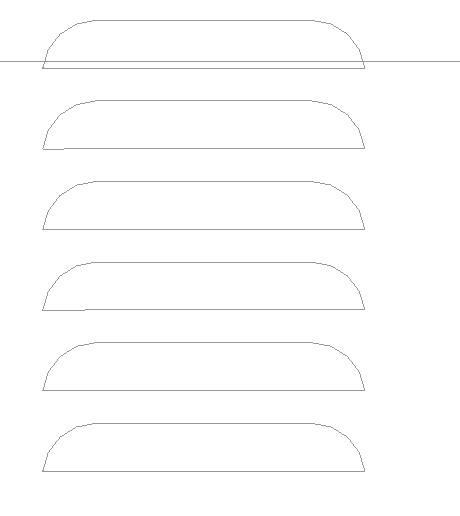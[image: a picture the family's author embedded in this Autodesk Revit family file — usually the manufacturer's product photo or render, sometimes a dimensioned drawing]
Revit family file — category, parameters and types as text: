
# Revit family: AquaMaster-Inverter_ENG-RFA-2022
name_source: partatom
category: Mechanické zařízení
units: mm (PartAtom-declared; Revit-internal decimal feet)

## family parameters
Bod výpočtu místnosti = Ne
Kóta kulaté spojky = Použít průměr
Nadpis OmniClass = Climate Control (HVAC)
Ořezat dutým tvarem při načtení = Ne
Sdílené = Ne
Typ dílu = Normální
Vždy vertikální = Ano
Zachovat orientaci poznámky = Ne
Založené na pracovní rovině = Ne
Číslo OmniClass = 23.75.00.00

## types (8) — shared parameters
MT_active power = 0 W
MT_angle offset = 60 mm  [stored 0.19685 ft]
MT_apparent power = 0 VA
MT_case mat = MT_RAL9006
MT_clearance back = 200 mm  [stored 0.656168 ft]
MT_clearance front = 600 mm
MT_frequency (Hz) = 50 Hz
MT_pipe connector mat = MT_RGB-130-130-130
MT_pipe mat = MT_angle-corner
Popis = Ground-to-water heat pump
Výrobce = Master Therm
zero-valued in all types: Cena, MT_CosPhi, Výchozí výška

## per-type parameters (varying)
- AQ45I: CI_hot water – inlet=1'' (OD); CO_hot water – outlet=1'' (OD); Desuperheater – inlet/outlet=not available; EI_brine – inlet=5/4'' (OD); EO_brine – outlet=5/4'' (OD); El. connection=2xPG16; 4xPG13.5; Komentáře k typům=COMPRESSOR: BLDC Inverter; 30 – 90 rps; charge of POE oil – 1.3 l; max. op. current – 15 A; EVAPORATOR: PHE; AISI316; water flow (W/W) – 1.62 kg/s; min. flow – 1.48 kg/s; brine flow (B/W) – 0.89 kg/s; min. flow – 0.54 kg/s; temp. difference – 3 K; int. volume – 5.1 l; pump ext. head – 3.5 m; pump motor – 250 W; CONDENSER: PHE; AISI316; water flow – 0.62 kg/s; min. flow – 0.46 kg/s; temp. difference – 5 K; int. volume – 4.1 l; pump ext. head – 3.0 m; pump motor – 100 W; REFRIGERANT CIRCUIT: R410a (2.4 kg); AUX. HEATER (optional): 7.5 kW; CONTROLS: controller – pCO5; EEV – yes; water probe – yes; SHW probe/output – yes (2x); mixing probe/output – yes; outdoor probe – yes; dynamic set point – yes; refrigerant probe – 2xPT; POWER SUPPLY: 3x400 V; 50 Hz; max. current – 20 A; max. current, incl. aux. heater – 28 A; DIMENSIONS: hot water, brine – 1", 5/4" (OD); 120x56x72 cm; 170 kg; LIMITS: max. water overpress. – 0.25 MPa; max. refr. overpress. – 4.2 MPa; brine min./max.: -5/+20 °C; water min./max.: 20/60 °C; MT_CI diameter=28 mm  [stored 0.0918635 ft]; MT_CI offset_X=73 mm  [stored 0.239501 ft]; MT_CO diameter=28 mm  [stored 0.0918635 ft]; MT_CO offset_X=173 mm  [stored 0.567585 ft]; MT_EC AQ17I_YES=Ne; MT_EC-AQ90I_YES=Ne; MT_EC1 offset_X=25 mm  [stored 0.082021 ft]; MT_EC1 offset_Y=90 mm  [stored 0.295276 ft]; MT_EC2 offset_X=25 mm  [stored 0.082021 ft]; MT_EC2 offset_Y=60 mm  [stored 0.19685 ft]; MT_EC3 offset_X=25 mm  [stored 0.082021 ft]; MT_EC3 offset_Y=30 mm  [stored 0.0984252 ft]; MT_EC4 offset_X=421 mm  [stored 1.38123 ft]; MT_EC4 offset_Y=90 mm  [stored 0.295276 ft]; MT_EC5 offset_X=421 mm  [stored 1.38123 ft]; MT_EC5 offset_Y=60 mm  [stored 0.19685 ft]; MT_EC6 offset_X=421 mm  [stored 1.38123 ft]; MT_EC6 offset_Y=30 mm  [stored 0.0984252 ft]; MT_EC6_YES=Ano; MT_EI diameter=35 mm  [stored 0.114829 ft]; MT_EI offset_X=373 mm  [stored 1.22375 ft]; MT_EO diameter=35 mm  [stored 0.114829 ft]; MT_EO offset_X=273 mm  [stored 0.895669 ft]; MT_TYPE=45; MT_angle length_X=406 mm  [stored 1.33202 ft]; MT_angle length_Y=596 mm; MT_angle length_Z=1080 mm; MT_case depth=716 mm; MT_case height=1200 mm; MT_case width=526 mm  [stored 1.72572 ft]; MT_clearance left=400 mm  [stored 1.31234 ft]; MT_clearance right=400 mm  [stored 1.31234 ft]; MT_clearance top=1800 mm; MT_cover front_X=446 mm  [stored 1.46325 ft]; MT_cover front_Y=1120 mm; MT_cover side_X=636 mm; MT_cover side_Y=1120 mm; MT_cover top_X=446 mm  [stored 1.46325 ft]; MT_cover top_Y=636 mm; MT_desuperheater diameter=0 mm  [stored 0 ft]; MT_desuperheater offset_X=223 mm  [stored 0.731627 ft]; MT_desuperheater_YES=Ne; MT_lock offset_V=300 mm; MT_lower vent grille_YES=Ne; MT_max. current, incl. aux. heater (A)=28 A; MT_pipe connector angle=0.00°; MT_pipe connector offset=486 mm; MT_pipe connector_X=446 mm  [stored 1.46325 ft]; MT_pipe connector_Y=120 mm  [stored 0.393701 ft]; MT_pivot offset=0 mm  [stored 0 ft]; MT_power switch_YES=Ano; MT_upper center lock_YES=Ano; MT_upper vent grille offset_H=175 mm  [stored 0.574147 ft]; MT_upper vent grille offset_V=200 mm  [stored 0.656168 ft]; MT_vent grille_YES=Ano; MT_voltage (V)=400 V; MT_weight (kg)=170; Model=AquaMaster Inverter 45I; URL=https://mastertherm.cz
- AQ60I: CI_hot water – inlet=1'' (OD); CO_hot water – outlet=1'' (OD); Desuperheater – inlet/outlet=not available; EI_brine – inlet=5/4'' (OD); EO_brine – outlet=5/4'' (OD); El. connection=2xPG16; 4xPG13.5; Komentáře k typům=COMPRESSOR: BLDC Inverter Scroll; 30 – 100 rps; charge of POE oil – 1.4 l; max. op. current – 35 A; EVAPORATOR: PHE; AISI316; water flow (W/W) – 2.37 kg/s; min. flow – 2.09 kg/s; brine flow (B/W) – 1.31 kg/s; min. flow – 0.79 kg/s; temp. difference – 3 K; int. volume – 5.1 l; pump ext. head – 5.0 m; pump motor – 450 W; CONDENSER: PHE; AISI316; water flow – 0.92 kg/s; min. flow – 0.69 kg/s; temp. difference – 5 K; int. volume – 4.1 l; pump ext. head – 3.0 m; pump motor – 130 W; REFRIGERANT CIRCUIT: R410a (2.5 kg); AUX. HEATER (optional): 7.5 kW; CONTROLS: controller – pCO5; EEV – 1+1 (EVI); water probe – yes; SHW probe/output – yes (2x); mixing probe/output – yes; outdoor probe – yes; dynamic set point – yes; refrigerant probe – 2xPT; POWER SUPPLY: 3x400 V; 50 Hz; max. current – 25 A; max. current, incl. aux. heater – 35 A; DIMENSIONS: hot water, brine – 1", 5/4" (OD); 120x56x72 cm; 190 kg; LIMITS: max. water overpress. – 0.25 MPa; max. refr. overpress. – 4.2 MPa; brine min./max.: -5/+20 °C; water min./max.: 20/60 °C; MT_CI diameter=28 mm  [stored 0.0918635 ft]; MT_CI offset_X=73 mm  [stored 0.239501 ft]; MT_CO diameter=28 mm  [stored 0.0918635 ft]; MT_CO offset_X=173 mm  [stored 0.567585 ft]; MT_EC AQ17I_YES=Ne; MT_EC-AQ90I_YES=Ne; MT_EC1 offset_X=25 mm  [stored 0.082021 ft]; MT_EC1 offset_Y=90 mm  [stored 0.295276 ft]; MT_EC2 offset_X=25 mm  [stored 0.082021 ft]; MT_EC2 offset_Y=60 mm  [stored 0.19685 ft]; MT_EC3 offset_X=25 mm  [stored 0.082021 ft]; MT_EC3 offset_Y=30 mm  [stored 0.0984252 ft]; MT_EC4 offset_X=421 mm  [stored 1.38123 ft]; MT_EC4 offset_Y=90 mm  [stored 0.295276 ft]; MT_EC5 offset_X=421 mm  [stored 1.38123 ft]; MT_EC5 offset_Y=60 mm  [stored 0.19685 ft]; MT_EC6 offset_X=421 mm  [stored 1.38123 ft]; MT_EC6 offset_Y=30 mm  [stored 0.0984252 ft]; MT_EC6_YES=Ano; MT_EI diameter=35 mm  [stored 0.114829 ft]; MT_EI offset_X=373 mm  [stored 1.22375 ft]; MT_EO diameter=35 mm  [stored 0.114829 ft]; MT_EO offset_X=273 mm  [stored 0.895669 ft]; MT_TYPE=60; MT_angle length_X=406 mm  [stored 1.33202 ft]; MT_angle length_Y=596 mm; MT_angle length_Z=1080 mm; MT_case depth=716 mm; MT_case height=1200 mm; MT_case width=526 mm  [stored 1.72572 ft]; MT_clearance left=400 mm  [stored 1.31234 ft]; MT_clearance right=400 mm  [stored 1.31234 ft]; MT_clearance top=1800 mm; MT_cover front_X=446 mm  [stored 1.46325 ft]; MT_cover front_Y=1120 mm; MT_cover side_X=636 mm; MT_cover side_Y=1120 mm; MT_cover top_X=446 mm  [stored 1.46325 ft]; MT_cover top_Y=636 mm; MT_desuperheater diameter=0 mm  [stored 0 ft]; MT_desuperheater offset_X=223 mm  [stored 0.731627 ft]; MT_desuperheater_YES=Ne; MT_lock offset_V=300 mm; MT_lower vent grille_YES=Ne; MT_max. current, incl. aux. heater (A)=35 A; MT_pipe connector angle=0.00°; MT_pipe connector offset=486 mm; MT_pipe connector_X=446 mm  [stored 1.46325 ft]; MT_pipe connector_Y=120 mm  [stored 0.393701 ft]; MT_pivot offset=0 mm  [stored 0 ft]; MT_power switch_YES=Ano; MT_upper center lock_YES=Ano; MT_upper vent grille offset_H=175 mm  [stored 0.574147 ft]; MT_upper vent grille offset_V=200 mm  [stored 0.656168 ft]; MT_vent grille_YES=Ano; MT_voltage (V)=400 V; MT_weight (kg)=190; Model=AquaMaster Inverter 60I; URL=https://mastertherm.cz
- AQ90I: CI_hot water – inlet=5/4'' (OD); CO_hot water – outlet=5/4'' (OD); Desuperheater – inlet/outlet=2xCu Ø15 mm (ID); EI_brine – inlet=5/4'' (OD); EO_brine – outlet=5/4'' (OD); El. connection=2xPG21; 2xPG16; 4xPG13.5; Komentáře k typům=COMPRESSOR: BLDC Inverter Scroll; 30 – 150 rps; charge of POE oil – 1.4 l; max. op. current – 35 A; EVAPORATOR: PHE; AISI316; water flow (W/W) – 3.64 kg/s; min. flow – 3.15 kg/s; brine flow (B/W) – 2.09 kg/s; min. flow – 1.26 kg/s; temp. difference – 3 K; int. volume – 5.1 l; pump ext. head – 5.0 m; pump motor – 310 W; CONDENSER: PHE; AISI316; water flow – 1.50 kg/s; min. flow – 1.12 kg/s; temp. difference – 5 K; int. volume – 4.1 l; pump ext. head – 8.0 m; pump motor – 310 W; REFRIGERANT CIRCUIT: R410a (4.0 kg); AUX. HEATER (optional): 7.5 kW; CONTROLS: controller – pCO5; EEV – 1+1 (EVI); water probe – yes; SHW probe/output – yes (2x); mixing probe/output – yes; outdoor probe – yes; dynamic set point – yes; refrigerant probe – 2xPT; POWER SUPPLY: 3x400 V; 50 Hz; max. current – 40 A; max. current, incl. aux. heater – 50 A; DIMENSIONS: hot water, brine – 5/4", 5/4" (OD); 120x72x72 cm; 210 kg; LIMITS: max. water overpress. – 0.25 MPa; max. refr. overpress. – 4.2 MPa; brine min./max.: -5/+20 °C; water min./max.: 20/60 °C; MT_CI diameter=35 mm  [stored 0.114829 ft]; MT_CI offset_X=93 mm  [stored 0.305118 ft]; MT_CO diameter=35 mm  [stored 0.114829 ft]; MT_CO offset_X=243 mm  [stored 0.797244 ft]; MT_EC AQ17I_YES=Ne; MT_EC-AQ90I_YES=Ano; MT_EC1 offset_X=25 mm  [stored 0.082021 ft]; MT_EC1 offset_Y=90 mm  [stored 0.295276 ft]; MT_EC2 offset_X=25 mm  [stored 0.082021 ft]; MT_EC2 offset_Y=60 mm  [stored 0.19685 ft]; MT_EC3 offset_X=25 mm  [stored 0.082021 ft]; MT_EC3 offset_Y=30 mm  [stored 0.0984252 ft]; MT_EC4 offset_X=608 mm; MT_EC4 offset_Y=90 mm  [stored 0.295276 ft]; MT_EC5 offset_X=608 mm; MT_EC5 offset_Y=60 mm  [stored 0.19685 ft]; MT_EC6 offset_X=608 mm; MT_EC6 offset_Y=30 mm  [stored 0.0984252 ft]; MT_EC6_YES=Ano; MT_EI diameter=35 mm  [stored 0.114829 ft]; MT_EI offset_X=543 mm  [stored 1.7815 ft]; MT_EO diameter=35 mm  [stored 0.114829 ft]; MT_EO offset_X=393 mm  [stored 1.28937 ft]; MT_TYPE=90; MT_angle length_X=596 mm; MT_angle length_Y=596 mm; MT_angle length_Z=1080 mm; MT_case depth=716 mm; MT_case height=1200 mm; MT_case width=716 mm; MT_clearance left=400 mm  [stored 1.31234 ft]; MT_clearance right=400 mm  [stored 1.31234 ft]; MT_clearance top=1800 mm; MT_cover front_X=636 mm; MT_cover front_Y=1120 mm; MT_cover side_X=636 mm; MT_cover side_Y=1120 mm; MT_cover top_X=636 mm; MT_cover top_Y=636 mm; MT_desuperheater diameter=15 mm  [stored 0.0492126 ft]; MT_desuperheater offset_X=318 mm  [stored 1.04331 ft]; MT_desuperheater_YES=Ano; MT_lock offset_V=300 mm; MT_lower vent grille_YES=Ne; MT_max. current, incl. aux. heater (A)=50 A; MT_pipe connector angle=0.00°; MT_pipe connector offset=676 mm; MT_pipe connector_X=636 mm; MT_pipe connector_Y=120 mm  [stored 0.393701 ft]; MT_pivot offset=0 mm  [stored 0 ft]; MT_power switch_YES=Ano; MT_upper center lock_YES=Ano; MT_upper vent grille offset_H=175 mm  [stored 0.574147 ft]; MT_upper vent grille offset_V=200 mm  [stored 0.656168 ft]; MT_vent grille_YES=Ne; MT_voltage (V)=400 V; MT_weight (kg)=210; Model=AquaMaster Inverter 90I; URL=https://www.mastertherm.eu
- AQ17I: CI_hot water – inlet=1'' (OD); CO_hot water – outlet=1'' (OD); Desuperheater – inlet/outlet=not available; EI_brine – inlet=1'' (OD); EO_brine – outlet=1'' (OD); El. connection=2xPG16; 4xPG13.5; Komentáře k typům=COMPRESSOR: BLDC Inverter; 15 – 65 rps; charge of POE oil – 0.9 l; max. op. current – 16 A; EVAPORATOR: PHE; AISI316; water flow (W/W) – 0.38 kg/s; min. flow – 0.28 kg/s; brine flow (B/W) – 0.19 kg/s; min. flow – 0.11 kg/s; temp. difference – 3 K; int. volume – 2.0 l; pump ext. head – 7.0 m; pump motor – 70 W; CONDENSER: PHE; AISI316; water flow – 0.14 kg/s; min. flow – 0.09 kg/s; temp. difference – 5 K; int. volume – 4.1 l; pump ext. head – 7.0 m; pump motor – 70 W; REFRIGERANT CIRCUIT: R410a (0.75 kg); AUX. HEATER (optional): not available; CONTROLS: controller – uPC; EEV – yes; water probe – yes; SHW probe/output – no; mixing probe/output – yes; outdoor probe – yes; dynamic set point – yes; refrigerant probe – 2xPT; POWER SUPPLY: 1x230 V; 50 Hz; max. current – 16 A; DIMENSIONS: hot water, brine – 1", 1" (OD); 82x53x53 cm; 60 kg; LIMITS: max. water overpress. – 0.25 MPa; max. refr. overpress. – 4.2 MPa; brine min./max.: -5/+20 °C; water min./max.: 20/60 °C; MT_CI diameter=28 mm  [stored 0.0918635 ft]; MT_CI offset_X=440 mm  [stored 1.44357 ft]; MT_CO diameter=28 mm  [stored 0.0918635 ft]; MT_CO offset_X=660 mm; MT_EC AQ17I_YES=Ano; MT_EC-AQ90I_YES=Ne; MT_EC1 offset_X=330 mm; MT_EC1 offset_Y=403 mm  [stored 1.32218 ft]; MT_EC2 offset_X=410 mm  [stored 1.34514 ft]; MT_EC2 offset_Y=403 mm  [stored 1.32218 ft]; MT_EC3 offset_X=480 mm  [stored 1.5748 ft]; MT_EC3 offset_Y=403 mm  [stored 1.32218 ft]; MT_EC4 offset_X=560 mm  [stored 1.83727 ft]; MT_EC4 offset_Y=403 mm  [stored 1.32218 ft]; MT_EC5 offset_X=630 mm; MT_EC5 offset_Y=403 mm  [stored 1.32218 ft]; MT_EC6 offset_X=421 mm  [stored 1.38123 ft]; MT_EC6 offset_Y=403 mm  [stored 1.32218 ft]; MT_EC6_YES=Ne; MT_EI diameter=28 mm  [stored 0.0918635 ft]; MT_EI offset_X=320 mm  [stored 1.04987 ft]; MT_EO diameter=28 mm  [stored 0.0918635 ft]; MT_EO offset_X=100 mm  [stored 0.328084 ft]; MT_TYPE=17; MT_angle length_X=406 mm  [stored 1.33202 ft]; MT_angle length_Y=406 mm  [stored 1.33202 ft]; MT_angle length_Z=680 mm; MT_case depth=526 mm  [stored 1.72572 ft]; MT_case height=800 mm; MT_case width=526 mm  [stored 1.72572 ft]; MT_clearance left=200 mm  [stored 0.656168 ft]; MT_clearance right=600 mm; MT_clearance top=1400 mm; MT_cover front_X=446 mm  [stored 1.46325 ft]; MT_cover front_Y=720 mm; MT_cover side_X=446 mm  [stored 1.46325 ft]; MT_cover side_Y=720 mm; MT_cover top_X=446 mm  [stored 1.46325 ft]; MT_cover top_Y=446 mm  [stored 1.46325 ft]; MT_desuperheater diameter=0 mm  [stored 0 ft]; MT_desuperheater offset_X=360 mm; MT_desuperheater_YES=Ne; MT_lock offset_V=400 mm  [stored 1.31234 ft]; MT_lower vent grille_YES=Ano; MT_max. current, incl. aux. heater (A)=16 A; MT_pipe connector angle=90.00°; MT_pipe connector offset=760 mm; MT_pipe connector_X=720 mm; MT_pipe connector_Y=85 mm  [stored 0.278871 ft]; MT_pivot offset=526 mm  [stored 1.72572 ft]; MT_power switch_YES=Ne; MT_upper center lock_YES=Ne; MT_upper vent grille offset_H=293 mm; MT_upper vent grille offset_V=150 mm; MT_vent grille_YES=Ano; MT_voltage (V)=230 V; MT_weight (kg)=60; Model=AquaMaster Inverter 17I; URL=https://mastertherm.cz
- AQ22I: CI_hot water – inlet=1'' (OD); CO_hot water – outlet=1'' (OD); Desuperheater – inlet/outlet=not available; EI_brine – inlet=1'' (OD); EO_brine – outlet=1'' (OD); El. connection=2xPG16; 4xPG13.5; Komentáře k typům=COMPRESSOR: BLDC Inverter; 30 – 100 rps; charge of POE oil – 1.3 l; max. op. current – 16 A; EVAPORATOR: PHE; AISI316; water flow (W/W) – 0.50 kg/s; min. flow – 0.44 kg/s; brine flow (B/W) – 0.28 kg/s; min. flow – 0.17 kg/s; temp. difference – 3 K; int. volume – 5.1 l; pump ext. head – 3.0 m; pump motor – 100 W; CONDENSER: PHE; AISI316; water flow – 0.20 kg/s; min. flow – 0.15 kg/s; temp. difference – 5 K; int. volume – 4.1 l; pump ext. head – 3.0 m; pump motor – 100 W; REFRIGERANT CIRCUIT: R410a (1.5 kg); AUX. HEATER (optional): 3 – 4 kW (4.5 – 6 kW bez kompresoru); CONTROLS: controller – pCO5; EEV – yes; water probe – yes; SHW probe/output – yes (2x); mixing probe/output – yes; outdoor probe – yes; dynamic set point – yes; refrigerant probe – 2xPT; POWER SUPPLY: 1x230 (3x400) V; 50 Hz; max. current – 16/0/0 A; max. current, incl. aux. heater – 16/10/10 A; DIMENSIONS: hot water, brine – 1", 1" (OD); 120x56x72 cm; 160 kg; LIMITS: max. water overpress. – 0.25 MPa; max. refr. overpress. – 4.2 MPa; brine min./max.: -5/+20 °C; water min./max.: 20/60 °C; MT_CI diameter=28 mm  [stored 0.0918635 ft]; MT_CI offset_X=73 mm  [stored 0.239501 ft]; MT_CO diameter=28 mm  [stored 0.0918635 ft]; MT_CO offset_X=173 mm  [stored 0.567585 ft]; MT_EC AQ17I_YES=Ne; MT_EC-AQ90I_YES=Ne; MT_EC1 offset_X=25 mm  [stored 0.082021 ft]; MT_EC1 offset_Y=90 mm  [stored 0.295276 ft]; MT_EC2 offset_X=25 mm  [stored 0.082021 ft]; MT_EC2 offset_Y=60 mm  [stored 0.19685 ft]; MT_EC3 offset_X=25 mm  [stored 0.082021 ft]; MT_EC3 offset_Y=30 mm  [stored 0.0984252 ft]; MT_EC4 offset_X=421 mm  [stored 1.38123 ft]; MT_EC4 offset_Y=90 mm  [stored 0.295276 ft]; MT_EC5 offset_X=421 mm  [stored 1.38123 ft]; MT_EC5 offset_Y=60 mm  [stored 0.19685 ft]; MT_EC6 offset_X=421 mm  [stored 1.38123 ft]; MT_EC6 offset_Y=30 mm  [stored 0.0984252 ft]; MT_EC6_YES=Ano; MT_EI diameter=28 mm  [stored 0.0918635 ft]; MT_EI offset_X=373 mm  [stored 1.22375 ft]; MT_EO diameter=28 mm  [stored 0.0918635 ft]; MT_EO offset_X=273 mm  [stored 0.895669 ft]; MT_TYPE=22; MT_angle length_X=406 mm  [stored 1.33202 ft]; MT_angle length_Y=596 mm; MT_angle length_Z=1080 mm; MT_case depth=716 mm; MT_case height=1200 mm; MT_case width=526 mm  [stored 1.72572 ft]; MT_clearance left=400 mm  [stored 1.31234 ft]; MT_clearance right=400 mm  [stored 1.31234 ft]; MT_clearance top=1800 mm; MT_cover front_X=446 mm  [stored 1.46325 ft]; MT_cover front_Y=1120 mm; MT_cover side_X=636 mm; MT_cover side_Y=1120 mm; MT_cover top_X=446 mm  [stored 1.46325 ft]; MT_cover top_Y=636 mm; MT_desuperheater diameter=0 mm  [stored 0 ft]; MT_desuperheater offset_X=223 mm  [stored 0.731627 ft]; MT_desuperheater_YES=Ne; MT_lock offset_V=300 mm; MT_lower vent grille_YES=Ne; MT_max. current, incl. aux. heater (A)=16 A; MT_pipe connector angle=0.00°; MT_pipe connector offset=486 mm; MT_pipe connector_X=446 mm  [stored 1.46325 ft]; MT_pipe connector_Y=120 mm  [stored 0.393701 ft]; MT_pivot offset=0 mm  [stored 0 ft]; MT_power switch_YES=Ano; MT_upper center lock_YES=Ano; MT_upper vent grille offset_H=175 mm  [stored 0.574147 ft]; MT_upper vent grille offset_V=200 mm  [stored 0.656168 ft]; MT_vent grille_YES=Ano; MT_voltage (V)=230 V; MT_weight (kg)=160; Model=AquaMaster Inverter 22I; URL=https://mastertherm.cz
- AQ26I: CI_hot water – inlet=1'' (OD); CO_hot water – outlet=1'' (OD); Desuperheater – inlet/outlet=not available; EI_brine – inlet=1'' (OD); EO_brine – outlet=1'' (OD); El. connection=2xPG16; 4xPG13.5; Komentáře k typům=COMPRESSOR: BLDC Inverter; 20 – 75 rps; charge of POE oil – 0.9 l; max. op. current – 20 A; EVAPORATOR: PHE; AISI316; water flow (W/W) – 1.03 kg/s; min. flow – 0.77 kg/s; brine flow (B/W) – 0.48 kg/s; min. flow – 0.29 kg/s; temp. difference – 3 K; int. volume – 5.1 l; pump ext. head – 4.0 m; pump motor – 70 W; CONDENSER: PHE; AISI316; water flow – 0.36 kg/s; min. flow – 0.25 kg/s; temp. difference – 5 K; int. volume – 4.1 l; pump ext. head – 6.0 m; pump motor – 70 W; REFRIGERANT CIRCUIT: R410a (1.3 kg); AUX. HEATER (optional): 3 – 4 kW (4.5 – 6 kW bez kompresoru); CONTROLS: controller – pCO5; EEV – yes; water probe – yes; SHW probe/output – yes (2x); mixing probe/output – yes; outdoor probe – yes; dynamic set point – yes; refrigerant probe – 2xPT; POWER SUPPLY: 1x230 (3x400) V; 50 Hz; max. current – 20/0/0 A; max. current, incl. aux. heater – 20/10/10 A; DIMENSIONS: hot water, brine – 1", 1" (OD); 120x56x72 cm; 160 kg; LIMITS: max. water overpress. – 0.25 MPa; max. refr. overpress. – 4.2 MPa; brine min./max.: -5/+20 °C; water min./max.: 20/60 °C; MT_CI diameter=28 mm  [stored 0.0918635 ft]; MT_CI offset_X=73 mm  [stored 0.239501 ft]; MT_CO diameter=28 mm  [stored 0.0918635 ft]; MT_CO offset_X=173 mm  [stored 0.567585 ft]; MT_EC AQ17I_YES=Ne; MT_EC-AQ90I_YES=Ne; MT_EC1 offset_X=25 mm  [stored 0.082021 ft]; MT_EC1 offset_Y=90 mm  [stored 0.295276 ft]; MT_EC2 offset_X=25 mm  [stored 0.082021 ft]; MT_EC2 offset_Y=60 mm  [stored 0.19685 ft]; MT_EC3 offset_X=25 mm  [stored 0.082021 ft]; MT_EC3 offset_Y=30 mm  [stored 0.0984252 ft]; MT_EC4 offset_X=421 mm  [stored 1.38123 ft]; MT_EC4 offset_Y=90 mm  [stored 0.295276 ft]; MT_EC5 offset_X=421 mm  [stored 1.38123 ft]; MT_EC5 offset_Y=60 mm  [stored 0.19685 ft]; MT_EC6 offset_X=421 mm  [stored 1.38123 ft]; MT_EC6 offset_Y=30 mm  [stored 0.0984252 ft]; MT_EC6_YES=Ano; MT_EI diameter=28 mm  [stored 0.0918635 ft]; MT_EI offset_X=373 mm  [stored 1.22375 ft]; MT_EO diameter=28 mm  [stored 0.0918635 ft]; MT_EO offset_X=273 mm  [stored 0.895669 ft]; MT_TYPE=26; MT_angle length_X=406 mm  [stored 1.33202 ft]; MT_angle length_Y=596 mm; MT_angle length_Z=1080 mm; MT_case depth=716 mm; MT_case height=1200 mm; MT_case width=526 mm  [stored 1.72572 ft]; MT_clearance left=400 mm  [stored 1.31234 ft]; MT_clearance right=400 mm  [stored 1.31234 ft]; MT_clearance top=1800 mm; MT_cover front_X=446 mm  [stored 1.46325 ft]; MT_cover front_Y=1120 mm; MT_cover side_X=636 mm; MT_cover side_Y=1120 mm; MT_cover top_X=446 mm  [stored 1.46325 ft]; MT_cover top_Y=636 mm; MT_desuperheater diameter=0 mm  [stored 0 ft]; MT_desuperheater offset_X=223 mm  [stored 0.731627 ft]; MT_desuperheater_YES=Ne; MT_lock offset_V=300 mm; MT_lower vent grille_YES=Ne; MT_max. current, incl. aux. heater (A)=20 A; MT_pipe connector angle=0.00°; MT_pipe connector offset=486 mm; MT_pipe connector_X=446 mm  [stored 1.46325 ft]; MT_pipe connector_Y=120 mm  [stored 0.393701 ft]; MT_pivot offset=0 mm  [stored 0 ft]; MT_power switch_YES=Ano; MT_upper center lock_YES=Ano; MT_upper vent grille offset_H=175 mm  [stored 0.574147 ft]; MT_upper vent grille offset_V=200 mm  [stored 0.656168 ft]; MT_vent grille_YES=Ano; MT_voltage (V)=230 V; MT_weight (kg)=160; Model=AquaMaster Inverter 26I; URL=https://mastertherm.cz
- AQ30I: CI_hot water – inlet=1'' (OD); CO_hot water – outlet=1'' (OD); Desuperheater – inlet/outlet=not available; EI_brine – inlet=1'' (OD); EO_brine – outlet=1'' (OD); El. connection=2xPG16; 4xPG13.5; Komentáře k typům=COMPRESSOR: BLDC Inverter; 30 – 90 rps; charge of POE oil – 0.75 l; max. op. current – 25 A; EVAPORATOR: PHE; AISI316; water flow (W/W) – 0.89 kg/s; min. flow – 0.79 kg/s; brine flow (B/W) – 0.50 kg/s; min. flow – 0.30 kg/s; temp. difference – 3 K; int. volume – 5.1 l; pump ext. head – 3.5 m; pump motor – 250 W; CONDENSER: PHE; AISI316; water flow – 0.34 kg/s; min. flow – 0.26 kg/s; temp. difference – 5 K; int. volume – 4.1 l; pump ext. head – 3.0 m; pump motor – 100 W; REFRIGERANT CIRCUIT: R410a (1.7 kg); AUX. HEATER (optional): 6 kW; CONTROLS: controller – pCO5; EEV – yes; water probe – yes; SHW probe/output – yes (2x); mixing probe/output – yes; outdoor probe – yes; dynamic set point – yes; refrigerant probe – 2xPT; POWER SUPPLY: 1x230 V; 50 Hz; max. current – 25 A; max. current, incl. aux. heater – 25 A; DIMENSIONS: hot water, brine – 1", 1" (OD); 120x56x72 cm; 160 kg; LIMITS: max. water overpress. – 0.25 MPa; max. refr. overpress. – 4.2 MPa; brine min./max.: -5/+20 °C; water min./max.: 20/60 °C; MT_CI diameter=28 mm  [stored 0.0918635 ft]; MT_CI offset_X=73 mm  [stored 0.239501 ft]; MT_CO diameter=28 mm  [stored 0.0918635 ft]; MT_CO offset_X=173 mm  [stored 0.567585 ft]; MT_EC AQ17I_YES=Ne; MT_EC-AQ90I_YES=Ne; MT_EC1 offset_X=25 mm  [stored 0.082021 ft]; MT_EC1 offset_Y=90 mm  [stored 0.295276 ft]; MT_EC2 offset_X=25 mm  [stored 0.082021 ft]; MT_EC2 offset_Y=60 mm  [stored 0.19685 ft]; MT_EC3 offset_X=25 mm  [stored 0.082021 ft]; MT_EC3 offset_Y=30 mm  [stored 0.0984252 ft]; MT_EC4 offset_X=421 mm  [stored 1.38123 ft]; MT_EC4 offset_Y=90 mm  [stored 0.295276 ft]; MT_EC5 offset_X=421 mm  [stored 1.38123 ft]; MT_EC5 offset_Y=60 mm  [stored 0.19685 ft]; MT_EC6 offset_X=421 mm  [stored 1.38123 ft]; MT_EC6 offset_Y=30 mm  [stored 0.0984252 ft]; MT_EC6_YES=Ano; MT_EI diameter=28 mm  [stored 0.0918635 ft]; MT_EI offset_X=373 mm  [stored 1.22375 ft]; MT_EO diameter=28 mm  [stored 0.0918635 ft]; MT_EO offset_X=273 mm  [stored 0.895669 ft]; MT_TYPE=30; MT_angle length_X=406 mm  [stored 1.33202 ft]; MT_angle length_Y=596 mm; MT_angle length_Z=1080 mm; MT_case depth=716 mm; MT_case height=1200 mm; MT_case width=526 mm  [stored 1.72572 ft]; MT_clearance left=400 mm  [stored 1.31234 ft]; MT_clearance right=400 mm  [stored 1.31234 ft]; MT_clearance top=1800 mm; MT_cover front_X=446 mm  [stored 1.46325 ft]; MT_cover front_Y=1120 mm; MT_cover side_X=636 mm; MT_cover side_Y=1120 mm; MT_cover top_X=446 mm  [stored 1.46325 ft]; MT_cover top_Y=636 mm; MT_desuperheater diameter=0 mm  [stored 0 ft]; MT_desuperheater offset_X=223 mm  [stored 0.731627 ft]; MT_desuperheater_YES=Ne; MT_lock offset_V=300 mm; MT_lower vent grille_YES=Ne; MT_max. current, incl. aux. heater (A)=25 A; MT_pipe connector angle=0.00°; MT_pipe connector offset=486 mm; MT_pipe connector_X=446 mm  [stored 1.46325 ft]; MT_pipe connector_Y=120 mm  [stored 0.393701 ft]; MT_pivot offset=0 mm  [stored 0 ft]; MT_power switch_YES=Ano; MT_upper center lock_YES=Ano; MT_upper vent grille offset_H=175 mm  [stored 0.574147 ft]; MT_upper vent grille offset_V=200 mm  [stored 0.656168 ft]; MT_vent grille_YES=Ano; MT_voltage (V)=230 V; MT_weight (kg)=160; Model=AquaMaster Inverter 30I; URL=https://mastertherm.cz
- AQ37I: CI_hot water – inlet=1'' (OD); CO_hot water – outlet=1'' (OD); Desuperheater – inlet/outlet=not available; EI_brine – inlet=1'' (OD); EO_brine – outlet=1'' (OD); El. connection=2xPG16; 4xPG13.5; Komentáře k typům=COMPRESSOR: BLDC Inverter; 20 – 100 rps; charge of POE oil – 0.95 l; max. op. current – 16 A; EVAPORATOR: PHE; AISI316; water flow (W/W) – 1.44 kg/s; min. flow – 1.08 kg/s; brine flow (B/W) – 0.67 kg/s; min. flow – 0.40 kg/s; temp. difference – 3 K; int. volume – 5.1 l; pump ext. head – 5.0 m; pump motor – 130 W; CONDENSER: PHE; AISI316; water flow – 0.46 kg/s; min. flow – 0.35 kg/s; temp. difference – 5 K; int. volume – 4.1 l; pump ext. head – 5.0 m; pump motor – 70 W; REFRIGERANT CIRCUIT: R410a (1.7 kg); AUX. HEATER (optional): 7.5 kW; CONTROLS: controller – pCO5; EEV – yes; water probe – yes; SHW probe/output – yes (2x); mixing probe/output – yes; outdoor probe – yes; dynamic set point – yes; refrigerant probe – 2xPT; POWER SUPPLY: 3x400 V; 50 Hz; max. current – 17 A; max. current, incl. aux. heater – 22 A; DIMENSIONS: hot water, brine – 1", 1" (OD); 120x56x72 cm; 165 kg; LIMITS: max. water overpress. – 0.25 MPa; max. refr. overpress. – 4.2 MPa; brine min./max.: -5/+20 °C; water min./max.: 20/60 °C; MT_CI diameter=28 mm  [stored 0.0918635 ft]; MT_CI offset_X=73 mm  [stored 0.239501 ft]; MT_CO diameter=28 mm  [stored 0.0918635 ft]; MT_CO offset_X=173 mm  [stored 0.567585 ft]; MT_EC AQ17I_YES=Ne; MT_EC-AQ90I_YES=Ne; MT_EC1 offset_X=25 mm  [stored 0.082021 ft]; MT_EC1 offset_Y=90 mm  [stored 0.295276 ft]; MT_EC2 offset_X=25 mm  [stored 0.082021 ft]; MT_EC2 offset_Y=60 mm  [stored 0.19685 ft]; MT_EC3 offset_X=25 mm  [stored 0.082021 ft]; MT_EC3 offset_Y=30 mm  [stored 0.0984252 ft]; MT_EC4 offset_X=421 mm  [stored 1.38123 ft]; MT_EC4 offset_Y=90 mm  [stored 0.295276 ft]; MT_EC5 offset_X=421 mm  [stored 1.38123 ft]; MT_EC5 offset_Y=60 mm  [stored 0.19685 ft]; MT_EC6 offset_X=421 mm  [stored 1.38123 ft]; MT_EC6 offset_Y=30 mm  [stored 0.0984252 ft]; MT_EC6_YES=Ano; MT_EI diameter=28 mm  [stored 0.0918635 ft]; MT_EI offset_X=373 mm  [stored 1.22375 ft]; MT_EO diameter=28 mm  [stored 0.0918635 ft]; MT_EO offset_X=273 mm  [stored 0.895669 ft]; MT_TYPE=37; MT_angle length_X=406 mm  [stored 1.33202 ft]; MT_angle length_Y=596 mm; MT_angle length_Z=1080 mm; MT_case depth=716 mm; MT_case height=1200 mm; MT_case width=526 mm  [stored 1.72572 ft]; MT_clearance left=400 mm  [stored 1.31234 ft]; MT_clearance right=400 mm  [stored 1.31234 ft]; MT_clearance top=1800 mm; MT_cover front_X=446 mm  [stored 1.46325 ft]; MT_cover front_Y=1120 mm; MT_cover side_X=636 mm; MT_cover side_Y=1120 mm; MT_cover top_X=446 mm  [stored 1.46325 ft]; MT_cover top_Y=636 mm; MT_desuperheater diameter=0 mm  [stored 0 ft]; MT_desuperheater offset_X=223 mm  [stored 0.731627 ft]; MT_desuperheater_YES=Ne; MT_lock offset_V=300 mm; MT_lower vent grille_YES=Ne; MT_max. current, incl. aux. heater (A)=22 A; MT_pipe connector angle=0.00°; MT_pipe connector offset=486 mm; MT_pipe connector_X=446 mm  [stored 1.46325 ft]; MT_pipe connector_Y=120 mm  [stored 0.393701 ft]; MT_pivot offset=0 mm  [stored 0 ft]; MT_power switch_YES=Ano; MT_upper center lock_YES=Ano; MT_upper vent grille offset_H=175 mm  [stored 0.574147 ft]; MT_upper vent grille offset_V=200 mm  [stored 0.656168 ft]; MT_vent grille_YES=Ano; MT_voltage (V)=400 V; MT_weight (kg)=165; Model=AquaMaster Inverter 37I; URL=https://mastertherm.cz

note: [stored X ft] marks values corroborated as IEEE doubles in the binary element streams (Revit-internal decimal feet)
